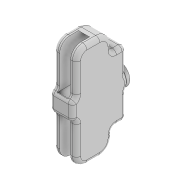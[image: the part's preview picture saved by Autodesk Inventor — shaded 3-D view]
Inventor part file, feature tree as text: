
AUTODESK INVENTOR PART (.ipt)
format: ipt  version: 2020.3 (Build 243373010, 373A)  size: 399,872 bytes
history: native  units: mm
features: sketch x7, extrude x6, fillet x3, projected_geometry x2, chamfer x1
ambient origin geometry x8: Origin, YZ Plane, XZ Plane, XY Plane, X Axis, Y Axis, Z Axis, Center Point
bodies: Solid1 (feature_tree)
feature tree (19):
  extrude  "Extrusion1"  Depth=20.25mm
  extrude  "Extrusion2"  Depth=20.0mm
  extrude  "Extrusion3"  Depth=92.5mm
  fillet  "Fillet1"  Radius=250.0mm
  extrude  "Extrusion4"  Depth=35.0mm
  extrude  "Extrusion5"  Depth=50.0mm
  sketch  "Sketch6"  dims[d18=30.0mm d19=55.0mm d20=0.0mm d21=5.0mm d22=26.5mm d23=0.0mm]
  extrude  "Extrusion6"  Depth=55.0mm TaperAngle=0.0deg
  fillet  "Fillet2"  Radius=5.0mm
  fillet  "Fillet3"  Radius=26.5mm
  chamfer  "Chamfer1"  Distance=2.0mm
  sketch  "Sketch1"  dims[d0=52.5mm d1=20.25mm]
  sketch  "Sketch2"  dims[d2=10.0mm d3=0.0mm d4=20.0mm]
  sketch  "Sketch3"  dims[d5=20.0mm d6=92.5mm d7=250.0mm]
  projected_geometry  "Projected Loop1"
  sketch  "Sketch4"  dims[d8=120.0mm d12=35.0mm]
  sketch  "Sketch5"  dims[d14=50.0mm d15=50.0mm]
  projected_geometry  "Projected Loop2"
  sketch  "Sketch7"  dims[d24=190.76mm d25=2.0mm d26=40.0mm d27=40.0mm d28=8.0mm d29=8.0mm d30=10.0mm d31=11.34464mm d34=50.0mm d35=112.5mm d36=0.0mm d37=10.0mm d38=0.0mm d39=10.0mm d40=0.0mm d41=10.0mm d42=10.0mm d43=10.0mm d44=5.0mm d45=2.0mm d46=45.0deg]
